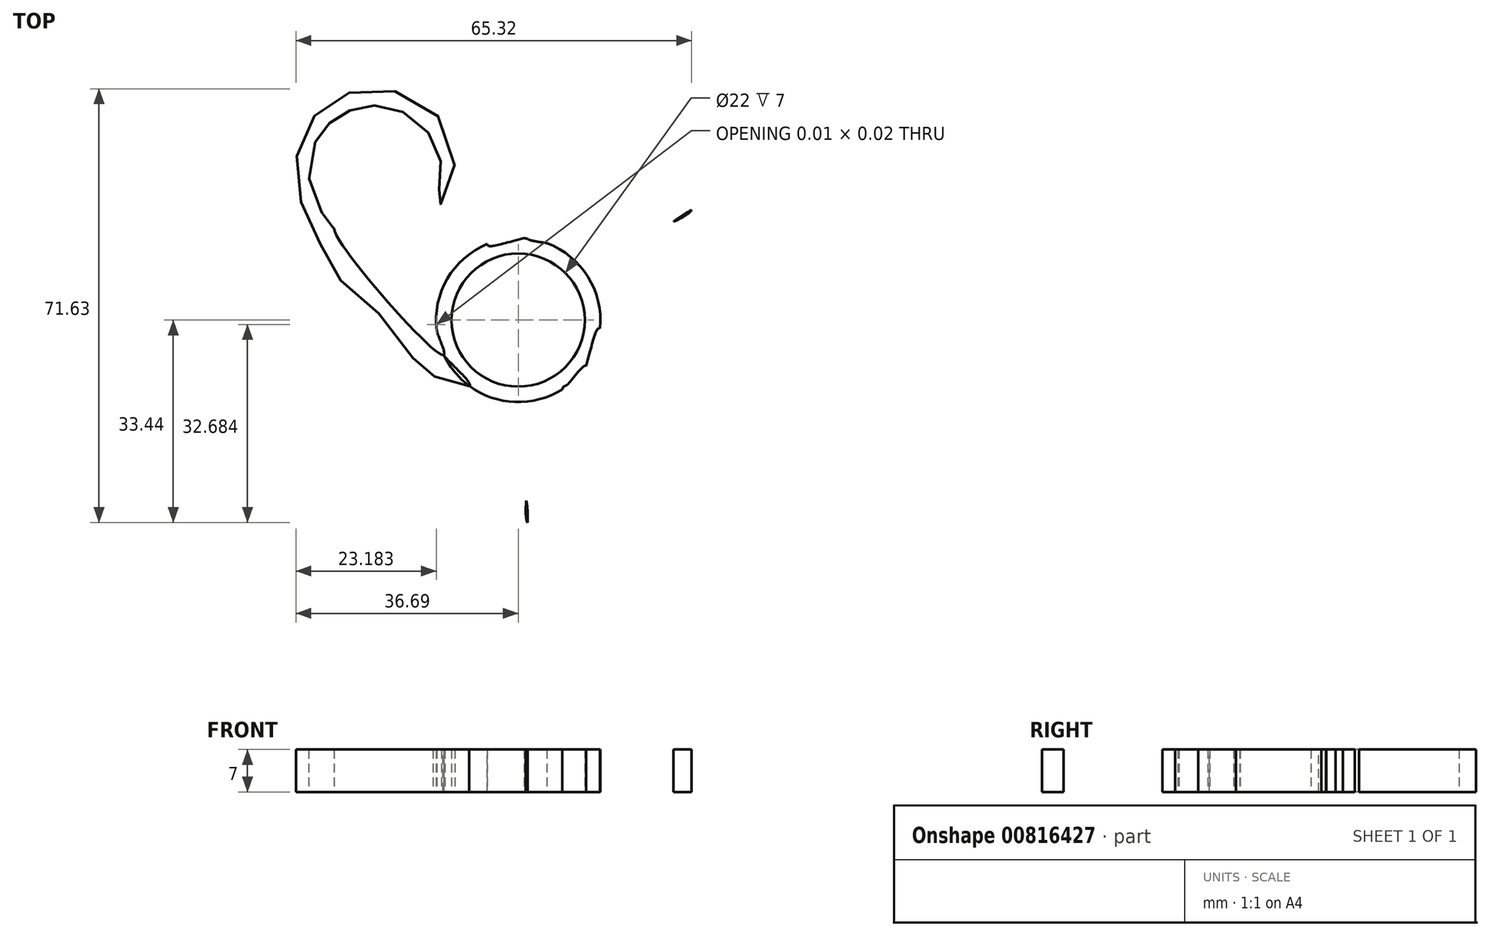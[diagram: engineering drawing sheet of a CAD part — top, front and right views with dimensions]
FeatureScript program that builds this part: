
annotation { "Feature Type Name" : "Feature", "Feature Type Description" : "" }
export const myFeature = defineFeature(function(context is Context, id is Id, definition is map)
    precondition{}
    {
        {
            var Q0;
            Q0=qCreatedBy(makeId("Top.planeOp"),FACE);
            var sketch = newSketch(context, id + "F0", { "sketchPlane" : qUnion([Q0])});
            skCircle(sketch, "E0", {"center": v(0, 0) * mm, "radius": 11 * mm});
            skCircle(sketch, "E1", {"center": v(0, 0) * mm, "radius": 13.55 * mm});
            skFitSpline(sketch, "E2.MirrorCS", {"points": [v(-12.38, -5.8) * mm, v(-32.41, 17.74) * mm, v(-34.3, 21.61) * mm, v(-34.36, 27.02) * mm, v(-33.17, 29.97) * mm, v(-32.16, 31.42) * mm, v(-31.02, 32.6) * mm, v(-29.6, 33.7) * mm, v(-27.75, 34.64) * mm, v(-26.22, 35.12) * mm, v(-23.71, 35.42) * mm, v(-21.09, 35.11) * mm, v(-18.3, 34.02) * mm, v(-15.44, 31.71) * mm, v(-13.62, 28.9) * mm, v(-12.79, 26) * mm, v(-12.68, 23.94) * mm, v(-13.41, 20.46) * mm, v(-14.07, 19.06) * mm, v(-12.41, 19.38) * mm, v(-10.48, 24.99) * mm, v(-12.96, 33.38) * mm, v(-19.92, 37.69) * mm, v(-26.92, 37.82) * mm, v(-32.12, 35.2) * mm, v(-35.65, 30.43) * mm, v(-36.65, 23.69) * mm, v(-34.9, 17.02) * mm, v(-31.84, 10.94) * mm, v(-29.04, 6.25) * mm, v(-22.41, 0.5) * mm, v(-16.78, -7.08) * mm, v(-14.99, -8.54) * mm, v(-12.34, -10.02) * mm, v(-8.12, -10.9) * mm, v(-12.38, -5.8) * mm]});
            skFitSpline(sketch, "E3.MirrorCS", {"points": [v(-13.47, -1.62) * mm, v(-13.51, -0.75) * mm, v(-18.86, 3.93) * mm, v(-23.64, 11.22) * mm, v(-30.37, 15.06) * mm, v(-12.38, -5.8) * mm, v(-13.47, -1.62) * mm]});
            skArc(sketch, "E4.MirrorCS", {"start": v(-26.7, 13.85) * mm, "mid": v(-29.82, 15.42) * mm, "end": v(-32.41, 17.74) * mm});
            skLineSegment(sketch, "E5", {"start": v(-13.51, -0.75) * mm, "end": v(-13.5, -0.77) * mm});
            skLineSegment(sketch, "E6.trimOffspring", {"start": v(-8.15, -10.83) * mm, "end": v(-8.12, -10.9) * mm});
            skFitSpline(sketch, "E7.MirrorCS", {"points": [v(1.45, 13.64) * mm, v(31.84, 19.22) * mm, v(36.14, 18.92) * mm, v(40.85, 16.27) * mm, v(42.81, 13.76) * mm, v(43.56, 12.16) * mm, v(44.02, 10.58) * mm, v(44.25, 8.8) * mm, v(44.14, 6.73) * mm, v(43.8, 5.17) * mm, v(42.8, 2.84) * mm, v(41.22, 0.72) * mm, v(38.88, -1.15) * mm, v(35.45, -2.47) * mm, v(32.1, -2.63) * mm, v(29.17, -1.9) * mm, v(27.34, -0.97) * mm, v(24.7, 1.4) * mm, v(23.8, 2.67) * mm, v(23.26, 1.08) * mm, v(27.15, -3.4) * mm, v(35.66, -5.45) * mm, v(42.87, -1.58) * mm, v(46.48, 4.42) * mm, v(46.82, 10.23) * mm, v(44.45, 15.68) * mm, v(39.1, 19.91) * mm, v(32.46, 21.74) * mm, v(25.66, 22.12) * mm, v(20.2, 22.04) * mm, v(11.9, 19.18) * mm, v(2.53, 18.09) * mm, v(0.37, 17.27) * mm, v(-2.24, 15.72) * mm, v(-5.1, 12.5) * mm, v(1.45, 13.64) * mm]});
            skFitSpline(sketch, "E8.MirrorCS", {"points": [v(5.6, 12.5) * mm, v(6.38, 12.1) * mm, v(13.1, 14.38) * mm, v(21.8, 14.88) * mm, v(28.5, 18.78) * mm, v(1.45, 13.64) * mm, v(5.6, 12.5) * mm]});
            skArc(sketch, "E9.MirrorCS", {"start": v(25.61, 16.22) * mm, "mid": v(28.53, 18.13) * mm, "end": v(31.84, 19.22) * mm});
            skFitSpline(sketch, "E10.MirrorCS", {"points": [v(11.18, -7.62) * mm, v(0.82, -36.73) * mm, v(-1.59, -40.31) * mm, v(-6.24, -43.06) * mm, v(-9.4, -43.5) * mm, v(-11.16, -43.35) * mm, v(-12.76, -42.96) * mm, v(-14.41, -42.27) * mm, v(-16.15, -41.14) * mm, v(-17.33, -40.06) * mm, v(-18.84, -38.04) * mm, v(-19.9, -35.6) * mm, v(-20.34, -32.64) * mm, v(-19.77, -29.02) * mm, v(-18.24, -26.03) * mm, v(-16.14, -23.86) * mm, v(-14.41, -22.75) * mm, v(-11.04, -21.64) * mm, v(-9.5, -21.5) * mm, v(-10.6, -20.23) * mm, v(-16.42, -21.36) * mm, v(-22.45, -27.7) * mm, v(-22.7, -35.89) * mm, v(-19.32, -42.02) * mm, v(-14.46, -45.21) * mm, v(-8.56, -45.88) * mm, v(-2.21, -43.37) * mm, v(2.69, -38.53) * mm, v(6.42, -32.83) * mm, v(9.09, -28.06) * mm, v(10.75, -19.45) * mm, v(14.5, -10.78) * mm, v(14.86, -8.5) * mm, v(14.83, -5.47) * mm, v(13.46, -1.37) * mm, v(11.18, -7.62) * mm]});
            skFitSpline(sketch, "E11.MirrorCS", {"points": [v(8.1, -10.65) * mm, v(7.38, -11.12) * mm, v(6, -18.09) * mm, v(2.08, -25.88) * mm, v(2.12, -33.62) * mm, v(11.18, -7.62) * mm, v(8.1, -10.65) * mm]});
            skArc(sketch, "E12.MirrorCS", {"start": v(1.33, -29.84) * mm, "mid": v(1.53, -33.32) * mm, "end": v(0.82, -36.73) * mm});
            skLineSegment(sketch, "E13", {"start": v(6.1, 12.1) * mm, "end": v(6.38, 12.1) * mm});
            skSolve(sketch);
        }
        {
            var Q0;
            Q0=makeQuery(id+"F0.imprint","IMPRINT",FACE,{"disambiguationData":[TD([[makeQuery(id+"F0.imprint","IMPRINT",EDGE,{"derivedFrom":sQuery(id+"F0.wireOp",EDGE,"E2.MirrorCS")}),1.0]])]});
            var Q1;
            Q1=makeQuery(id+"F0.imprint","IMPRINT",FACE,{"disambiguationData":[TD([[makeQuery(id+"F0.imprint","IMPRINT",EDGE,{"derivedFrom":sQuery(id+"F0.wireOp",EDGE,"E0")}),-1.0]])]});
            var Q2;
            {var subQ5=sQuery(id+"F0.wireOp",EDGE,"E12.MirrorCS");Q2=makeQuery(id+"F0.imprint","IMPRINT",FACE,{"disambiguationData":[TD([[makeQuery(id+"F0.imprint","IMPRINT",EDGE,{"derivedFrom":subQ5}),1.0]])]});}
            var Q3;
            {var subQ0=sQuery(id+"F0.wireOp",EDGE,"E9.MirrorCS");Q3=makeQuery(id+"F0.imprint","IMPRINT",FACE,{"disambiguationData":[TD([[makeQuery(id+"F0.imprint","IMPRINT",EDGE,{"derivedFrom":subQ0}),1.0]])]});}
            var Q4;
            Q4=makeQuery(id+"F0.imprint","IMPRINT",FACE,{"disambiguationData":[TD([[makeQuery(id+"F0.imprint","IMPRINT",EDGE,{"derivedFrom":sQuery(id+"F0.wireOp",EDGE,"E0")}),1.0]])]});
            var Q5;
            {var subQ4=sQuery(id+"F0.wireOp",EDGE,"E5");Q5=makeQuery(id+"F0.imprint","IMPRINT",FACE,{"disambiguationData":[TD([[makeQuery(id+"F0.imprint","IMPRINT",EDGE,{"derivedFrom":subQ4}),-1.0]])]});}
            extrude(context, id + "F1", {"entities" : qUnion([Q0, Q1, Q2, Q3, Q4, Q5]), "depth" : 7 * mm, "offsetDistance" : 25.4 * mm});
        }
        {
            var Q0;
            Q0=sQuery(id+"F0.wireOp",VERTEX,"E0.center");
            var Q1;
            Q1=makeQuery(id+"F1.opExtrude","SWEPT_BODY",BODY,{"disambiguationData":[OSD([sQuery(id+"F0.wireOp",EDGE,"E1"),sQuery(id+"F0.wireOp",EDGE,"E2.MirrorCS"),sQuery(id+"F0.wireOp",EDGE,"E3.MirrorCS"),sQuery(id+"F0.wireOp",EDGE,"E4.MirrorCS"),sQuery(id+"F0.wireOp",EDGE,"E6.trimOffspring"),sQuery(id+"F0.wireOp",EDGE,"E7.MirrorCS"),sQuery(id+"F0.wireOp",EDGE,"E8.MirrorCS"),sQuery(id+"F0.wireOp",EDGE,"E9.MirrorCS"),sQuery(id+"F0.wireOp",EDGE,"E10.MirrorCS"),sQuery(id+"F0.wireOp",EDGE,"E11.MirrorCS"),sQuery(id+"F0.wireOp",EDGE,"E12.MirrorCS"),sQuery(id+"F0.wireOp",EDGE,"E13")])]});
            hole(context, id + "F2", {"style" : HoleStyle.SIMPLE, "endStyle" : HoleEndStyle.THROUGH, "oppositeDirection" : true, "holeDiameter" : 22 * mm, "majorDiameter" : 6.35 * mm, "isTappedThrough" : true, "tappedDepth" : 12.7 * mm, "tapClearance" : 3, "locations" : qUnion([Q0]), "scope" : qUnion([Q1])});
        }
    });
